# Revit family: NOK2_63_UN_Surface-mounted_ETK
name_source: partatom
category: Lighting Fixtures
units: mm (PartAtom-declared; Revit-internal decimal feet)

## family parameters
Always vertical = Yes
Cut with Voids When Loaded = Yes
Light Source = Yes
OmniClass Number = 23.80.70.11.14.11
OmniClass Title = Downlights
Part Type = Normal
Room Calculation Point = Yes
Round Connector Dimension = Use Diameter
Shared = No
Work Plane-Based = No

## types (17) — shared parameters
Assembly Code = 63.0
Calc_LightSource = 180 mm  [stored 0.590551 ft]
Calc_Radius = 65 mm  [stored 0.213255 ft]
Calc_Symbol_Diameter = 1 mm  [stored 0.00328084 ft]
Color Filter = 16777215
D1 = 130 mm  [stored 0.426509 ft]
Dimming Lamp Color Temperature Shift = <None>
ETIM Code = -
GTIN Code = -
Housing_Material = Select RGB Value for different appearance
IK Value = -
IP Value = IP20
ISBN Code = -
IfcExportAs = IfcLightFixtureType
IfcExportType = USERDEFINED
L1 = 185 mm  [stored 0.606955 ft]
Lamp = LED
Manufacturer = ETK B.V.
Model = NOK.2
Tilt Angle = 90.00°
Type Comments = NOK.2 Delta
URL = https://www.ivlibrary.com
Voltage = 230 V

## per-type parameters (varying)
| type | Apparent Load | Luminous Flux (lm) | Photometric Web File | Wattage Comments |
| NOK.2 LED 38W 4000K 30 5300Lm CRI>80 zwart DALI 130x185 | 38 VA | 4247 lm | NOK.2403.31_LDT.ies | 38 |
| NOK.2 LED 38W 4000K 30 5300Lm CRI>80 wit DALI 130x185 | 38 VA | 4247 lm | NOK.2403.15_LDT.ies | 38 |
| NOK.2 LED 38W 4000K 30 5300Lm CRI>80 zwart 130x185 | 38 VA | 4247 lm | NOK.2400.31_LDT.ies | 38 |
| NOK.2 LED 38W 3000K 30 5165Lm CRI>80 zwart DALI 130x185 | 38 VA | 4099 lm | NOK.2303.31_LDT.ies | 38 |
| NOK.2 LED 38W 4000K 30 5300Lm CRI>80 wit 130x185 | 38 VA | 4247 lm | NOK.2400.15_LDT.ies | 38 |
| NOK.2 in NOOD LED 38W 3000K 30 450Lm CRI>80 wit DALI 130x185 | 38 VA | 350 lm | NOK.2303.15NV_LDT.ies | 38 |
| NOK.2 LED 38W 3000K 30 5165Lm CRI>80 wit DALI 130x185 | 38 VA | 4099 lm | NOK.2303.15_LDT.ies | 38 |
| NOK.2 LED 38W 3000K 30 5165Lm CRI>80 zwart 130x185 | 38 VA | 4099 lm | NOK.2300.31_LDT.ies | 38 |
| NOK.2 LED 38W 3000K 30 5165Lm CRI>80 wit 130x185 | 38 VA | 4099 lm | NOK.2300.15_LDT.ies | 38 |
| NOK.2 LED 32W 4000K 30 4620Lm CRI>80 zwart DALI 130x185 | 32 VA | 3718 lm | NOK.2203.31_LDT.ies | 32 |
| NOK.2 LED 32W 4000K 30 4620Lm CRI>80 wit DALI 130x185 | 32 VA | 3718 lm | NOK.2203.15_LDT.ies | 32 |
| NOK.2 LED 32W 4000K 30 4620Lm CRI>80 zwart 130x185 | 32 VA | 3718 lm | NOK.2200.31_LDT.ies | 32 |
| NOK.2 LED 32W 4000K 30 4620Lm CRI>80 wit 130x185 | 32 VA | 3718 lm | NOK.2200.15_LDT.ies | 32 |
| NOK.2 LED 32W 3000K 30 4500Lm CRI>80 zwart DALI  130x185 | 32 VA | 3605 lm | NOK.2103.31_LDT.ies | 32 |
| NOK.2 LED 32W 3000K 30 4500Lm CRI>80 wit DALI  130x185 | 32 VA | 3605 lm | NOK.2103.15_LDT.ies | 32 |
| NOK.2 LED 32W 3000K 30 4500Lm CRI>80 zwart 130x185 | 32 VA | 3605 lm | NOK.2100.31.ies | 32 |
| NOK.2 LED 32W 3000K 30 4500Lm CRI>80 wit 130x185 | 32 VA | 3605 lm | NOK.2100.15.ies | 32 |

note: [stored X ft] marks values corroborated as IEEE doubles in the binary element streams (Revit-internal decimal feet)

## geometry (parser evidence)
native form markers: Sweep x8
no freeform markers — native parametric forms only
